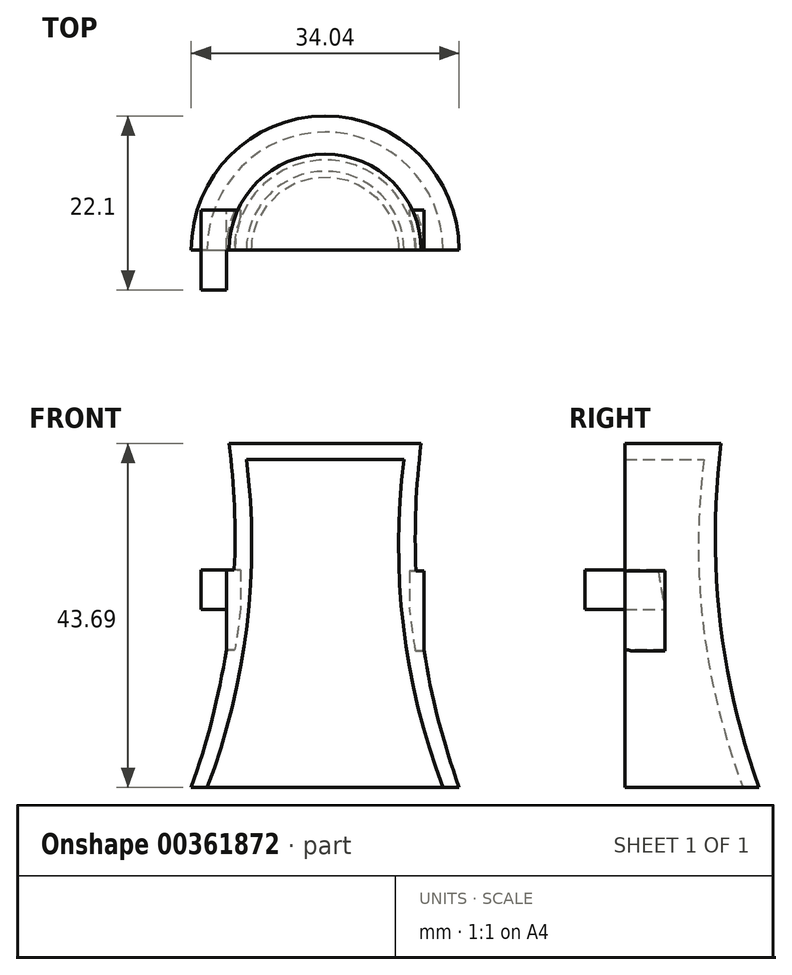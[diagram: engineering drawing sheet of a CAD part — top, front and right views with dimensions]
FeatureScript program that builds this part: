
annotation { "Feature Type Name" : "Feature", "Feature Type Description" : "" }
export const myFeature = defineFeature(function(context is Context, id is Id, definition is map)
    precondition{}
    {
        {
            var Q0;
            Q0=qCreatedBy(makeId("Front.planeOp"),FACE);
            var sketch = newSketch(context, id + "F0", { "sketchPlane" : qUnion([Q0])});
            skLineSegment(sketch, "E0", {"start": v(0, 9.22) * mm, "end": v(-12.2, 9.22) * mm});
            skLineSegment(sketch, "E1", {"start": v(0, 9.22) * mm, "end": v(0, 7.18) * mm});
            skLineSegment(sketch, "E2", {"start": v(-10, 7.18) * mm, "end": v(0, 7.18) * mm});
            skArc(sketch, "E3", {"start": v(-14.99, -34.47) * mm, "mid": v(-9.93, -13.95) * mm, "end": v(-10, 7.18) * mm});
            skLineSegment(sketch, "E4", {"start": v(-14.99, -34.47) * mm, "end": v(-17.02, -34.47) * mm});
            skArc(sketch, "E5", {"start": v(-17.02, -34.47) * mm, "mid": v(-12.02, -12.91) * mm, "end": v(-12.2, 9.22) * mm});
            skLineSegment(sketch, "E6", {"start": v(-12.55, -16.97) * mm, "end": v(-12.55, -6.8) * mm});
            skLineSegment(sketch, "E7", {"start": v(-12.55, -6.8) * mm, "end": v(-10.74, -6.8) * mm});
            skLineSegment(sketch, "E8", {"start": v(-10.74, -6.8) * mm, "end": v(-10.74, -16.97) * mm});
            skLineSegment(sketch, "E9", {"start": v(-10.74, -16.97) * mm, "end": v(-12.55, -16.97) * mm});
            skLineSegment(sketch, "E10.bottom", {"start": v(-12.55, -6.8) * mm, "end": v(-15.77, -6.8) * mm});
            skLineSegment(sketch, "E10.top", {"start": v(-12.55, -11.89) * mm, "end": v(-15.77, -11.89) * mm});
            skLineSegment(sketch, "E10.left", {"start": v(-12.55, -6.8) * mm, "end": v(-12.55, -11.89) * mm});
            skLineSegment(sketch, "E10.right", {"start": v(-15.77, -6.8) * mm, "end": v(-15.77, -11.89) * mm});
            skLineSegment(sketch, "E11.bottom", {"start": v(0, 9.22) * mm, "end": v(-5.1, 9.22) * mm});
            skLineSegment(sketch, "E11.top", {"start": v(0, 11.82) * mm, "end": v(-5.1, 11.82) * mm});
            skLineSegment(sketch, "E11.left", {"start": v(0, 9.22) * mm, "end": v(0, 11.82) * mm});
            skLineSegment(sketch, "E11.right", {"start": v(-5.1, 9.22) * mm, "end": v(-5.1, 11.82) * mm});
            skLineSegment(sketch, "E12.bottom", {"start": v(10.74, -6.98) * mm, "end": v(12.55, -6.98) * mm});
            skLineSegment(sketch, "E12.top", {"start": v(10.74, -17.14) * mm, "end": v(12.55, -17.14) * mm});
            skLineSegment(sketch, "E12.left", {"start": v(10.74, -6.98) * mm, "end": v(10.74, -17.14) * mm});
            skLineSegment(sketch, "E12.right", {"start": v(12.55, -6.98) * mm, "end": v(12.55, -17.14) * mm});
            skLineSegment(sketch, "E13.top", {"start": v(12.55, -12.05) * mm, "end": v(15.77, -12.05) * mm});
            skLineSegment(sketch, "E13.left", {"start": v(12.55, -6.98) * mm, "end": v(12.55, -12.05) * mm});
            skLineSegment(sketch, "E14.bottom", {"start": v(15.77, -12.05) * mm, "end": v(12.55, -12.05) * mm});
            skLineSegment(sketch, "E14.top", {"start": v(15.77, -17.14) * mm, "end": v(12.55, -17.14) * mm});
            skLineSegment(sketch, "E14.left", {"start": v(15.77, -12.05) * mm, "end": v(15.77, -17.14) * mm});
            skLineSegment(sketch, "E14.right", {"start": v(12.55, -12.05) * mm, "end": v(12.55, -17.14) * mm});
            skSolve(sketch);
        }
        {
            var Q0;
            {var subQ1=sQuery(id+"F0.wireOp",EDGE,"E0");Q0=makeQuery(id+"F0.imprint","IMPRINT",FACE,{"disambiguationData":[TD([[makeQuery(id+"F0.imprint","IMPRINT",EDGE,{"derivedFrom":subQ1}),1.0]])]});}
            var Q1;
            {var subQ4=sQuery(id+"F0.wireOp",EDGE,"E8");Q1=makeQuery(id+"F0.imprint","IMPRINT",FACE,{"disambiguationData":[TD([[makeQuery(id+"F0.imprint","IMPRINT",EDGE,{"derivedFrom":subQ4}),-1.0]])]});}
            var Q2;
            Q2=sQuery(id+"F0.wireOp",EDGE,"E1");
            revolve(context, id + "F1", {"entities" : qUnion([Q0, Q1]), "axis" : qUnion([Q2]), "revolveType" : RevolveType.ONE_DIRECTION, "angle" : 180 * degree});
        }
        {
            var Q0;
            {var subQ0=sQuery(id+"F0.wireOp",EDGE,"E6");Q0=makeQuery(id+"F0.imprint","IMPRINT",FACE,{"disambiguationData":[TD([[makeQuery(id+"F0.imprint","IMPRINT",EDGE,{"derivedFrom":subQ0}),-1.0]])]});}
            var Q1;
            {var subQ4=sQuery(id+"F0.wireOp",EDGE,"E8");Q1=makeQuery(id+"F0.imprint","IMPRINT",FACE,{"disambiguationData":[TD([[makeQuery(id+"F0.imprint","IMPRINT",EDGE,{"derivedFrom":subQ4}),-1.0]])]});}
            var Q2;
            Q2=makeQuery(id+"F0.imprint","IMPRINT",FACE,{"disambiguationData":[TD([[makeQuery(id+"F0.imprint","IMPRINT",EDGE,{"derivedFrom":sQuery(id+"F0.wireOp",EDGE,"E12.bottom")}),-1.0]])]});
            extrude(context, id + "F2", {"entities" : qUnion([Q0, Q1, Q2]), "operationType" : NewBodyOperationType.ADD, "depth" : -5.08 * mm});
        }
        {
            var Q0;
            Q0=makeQuery(id+"F0.imprint","IMPRINT",FACE,{"disambiguationData":[TD([[makeQuery(id+"F0.imprint","IMPRINT",EDGE,{"derivedFrom":sQuery(id+"F0.wireOp",EDGE,"E14.bottom")}),1.0]])]});
            var Q1;
            Q1=makeQuery(id+"F0.imprint","IMPRINT",FACE,{"disambiguationData":[TD([[makeQuery(id+"F0.imprint","IMPRINT",EDGE,{"derivedFrom":sQuery(id+"F0.wireOp",EDGE,"E10.bottom")}),1.0]])]});
            var Q2;
            Q2=makeQuery(id+"F0.imprint","IMPRINT",FACE,{"disambiguationData":[TD([[makeQuery(id+"F0.imprint","IMPRINT",EDGE,{"derivedFrom":sQuery(id+"F0.wireOp",EDGE,"E11.bottom")}),-1.0]])]});
            extrude(context, id + "F3", {"entities" : qUnion([Q0, Q1, Q2]), "operationType" : NewBodyOperationType.ADD, "depth" : 10.16 * mm, "symmetric" : true});
        }
    });
